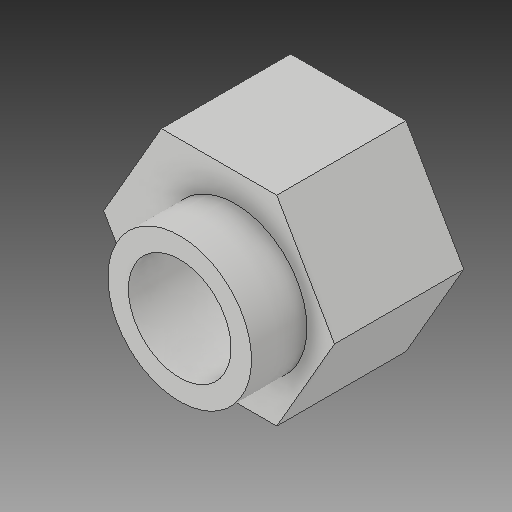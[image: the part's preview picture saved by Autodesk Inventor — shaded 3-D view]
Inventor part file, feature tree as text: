
AUTODESK INVENTOR PART (.ipt)
format: ipt  version: 2017 (Build 210142000, 142)  size: 121,344 bytes
history: native  units: mm
features: other x3, sketch x3
ambient origin geometry x8: Origin, YZ Plane, XZ Plane, XY Plane, X Axis, Y Axis, Z Axis, Center Point
bodies: Solid1 (feature_tree)
feature tree (6):
  other  "Eccentric Spacer_MIR.ipt"
  other  "Solid1::Eccentric Spacer_MIR.ipt"
  other  "TaggingFeature1"
  sketch  "Sketch1"  dims[d0=10.0mm]
  sketch  "Sketch2"
  sketch  "Sketch3"
